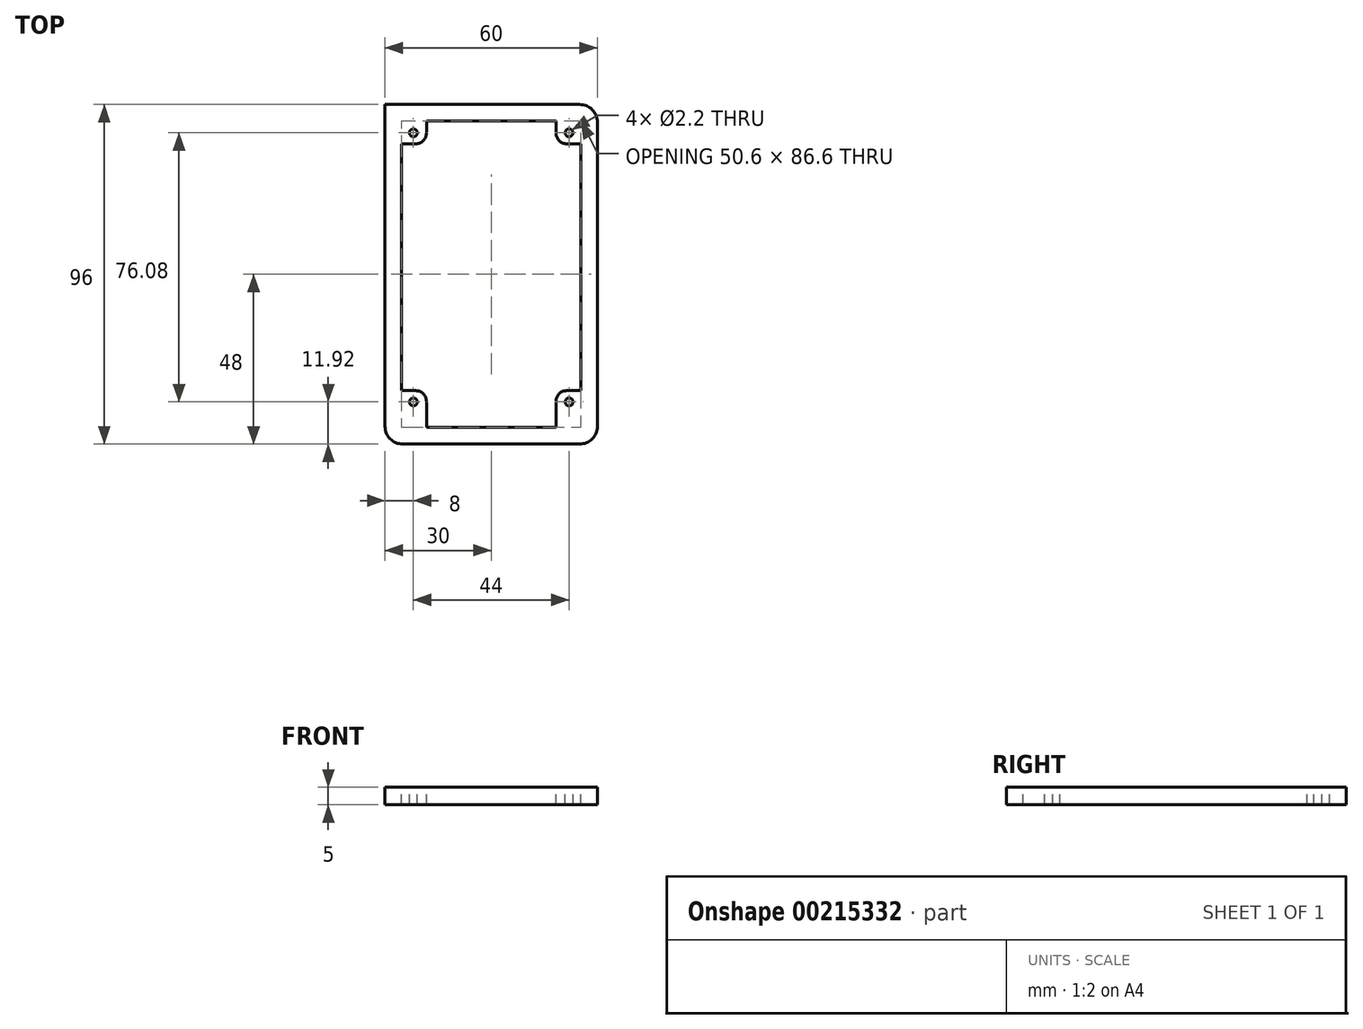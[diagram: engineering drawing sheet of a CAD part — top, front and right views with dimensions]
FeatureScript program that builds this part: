
annotation { "Feature Type Name" : "Feature", "Feature Type Description" : "" }
export const myFeature = defineFeature(function(context is Context, id is Id, definition is map)
    precondition{}
    {
        {
            var Q0;
            Q0=qCreatedBy(makeId("Top.planeOp"),FACE);
            var sketch = newSketch(context, id + "F0", { "sketchPlane" : qUnion([Q0])});
            skPoint(sketch, "E0.middle", {"position": v(0, 0) * mm});
            skCircle(sketch, "E1", {"center": v(-22, 40) * mm, "radius": 1.5 * mm});
            skCircle(sketch, "E2", {"center": v(22, 40) * mm, "radius": 1.5 * mm});
            skCircle(sketch, "E3", {"center": v(-22, -36.08) * mm, "radius": 1.5 * mm});
            skCircle(sketch, "E4", {"center": v(22, -36.08) * mm, "radius": 1.5 * mm});
            skLineSegment(sketch, "E5.bottom", {"start": v(25, -48) * mm, "end": v(-25, -48) * mm});
            skLineSegment(sketch, "E5.top", {"start": v(25, 48) * mm, "end": v(-27, 48) * mm});
            skLineSegment(sketch, "E5.left", {"start": v(30, -43) * mm, "end": v(30, 43) * mm});
            skLineSegment(sketch, "E5.right", {"start": v(-30, -43) * mm, "end": v(-30, 43) * mm});
            skPoint(sketch, "E6.visualSharp", {"position": v(-30, 48) * mm});
            skPoint(sketch, "E7.visualSharp", {"position": v(30, 48) * mm});
            skLineSegment(sketch, "E8.top", {"start": v(-30, 48) * mm, "end": v(-27, 48) * mm});
            skLineSegment(sketch, "E8.left", {"start": v(-30, 43) * mm, "end": v(-30, 48) * mm});
            skArc(sketch, "E9.filletArc", {"start": v(30, 43) * mm, "mid": v(28.54, 46.54) * mm, "end": v(25, 48) * mm});
            skPoint(sketch, "E10.visualSharp", {"position": v(30, -48) * mm});
            skArc(sketch, "E10.filletArc", {"start": v(25, -48) * mm, "mid": v(28.54, -46.54) * mm, "end": v(30, -43) * mm});
            skPoint(sketch, "E11.visualSharp", {"position": v(-30, -48) * mm});
            skArc(sketch, "E11.filletArc", {"start": v(-30, -43) * mm, "mid": v(-28.54, -46.54) * mm, "end": v(-25, -48) * mm});
            skSolve(sketch);
        }
        {
            var Q0;
            Q0=qSketchRegion(id+"F0",true);
            extrude(context, id + "F1", {"entities" : qUnion([Q0]), "depth" : 15 * mm});
        }
        {
            var Q0;
            Q0=makeQuery(id+"F1.opExtrude","CAP_FACE",FACE,{"disambiguationData":[OSD([sQuery(id+"F0.wireOp",EDGE,"E1"),sQuery(id+"F0.wireOp",EDGE,"E2"),sQuery(id+"F0.wireOp",EDGE,"E3"),sQuery(id+"F0.wireOp",EDGE,"E4"),sQuery(id+"F0.wireOp",EDGE,"E5.bottom"),sQuery(id+"F0.wireOp",EDGE,"E5.top"),sQuery(id+"F0.wireOp",EDGE,"E5.left"),sQuery(id+"F0.wireOp",EDGE,"E5.right")])],"isStart":false});
            var sketch = newSketch(context, id + "F2", { "sketchPlane" : qUnion([Q0])});
            skLineSegment(sketch, "E12.bottom", {"start": v(-25.3, 43.3) * mm, "end": v(25.3, 43.3) * mm});
            skLineSegment(sketch, "E12.top", {"start": v(-25.3, -43.3) * mm, "end": v(25.3, -43.3) * mm});
            skLineSegment(sketch, "E12.left", {"start": v(-25.3, 43.3) * mm, "end": v(-25.3, -43.3) * mm});
            skLineSegment(sketch, "E12.right", {"start": v(25.3, 43.3) * mm, "end": v(25.3, -43.3) * mm});
            skPoint(sketch, "E12.middle", {"position": v(0, 0) * mm});
            skCircle(sketch, "E13", {"center": v(-22, 40) * mm, "radius": 1.5 * mm});
            skCircle(sketch, "E14", {"center": v(22, 40) * mm, "radius": 1.5 * mm});
            skCircle(sketch, "E15", {"center": v(-22, -36.08) * mm, "radius": 1.5 * mm});
            skCircle(sketch, "E16", {"center": v(22, -36.08) * mm, "radius": 1.5 * mm});
            skSolve(sketch);
        }
        {
            var Q0;
            Q0=qSketchRegion(id+"F2",true);
            extrude(context, id + "F3", {"entities" : qUnion([Q0]), "operationType" : NewBodyOperationType.REMOVE, "oppositeDirection" : true, "depth" : 22 * mm});
        }
        {
            var Q0;
            Q0=makeQuery(id+"F1.opExtrude","CAP_FACE",FACE,{"disambiguationData":[OSD([sQuery(id+"F0.wireOp",EDGE,"E1"),sQuery(id+"F0.wireOp",EDGE,"E2"),sQuery(id+"F0.wireOp",EDGE,"E3"),sQuery(id+"F0.wireOp",EDGE,"E4"),sQuery(id+"F0.wireOp",EDGE,"E5.bottom"),sQuery(id+"F0.wireOp",EDGE,"E5.top"),sQuery(id+"F0.wireOp",EDGE,"E5.left"),sQuery(id+"F0.wireOp",EDGE,"E5.right")])],"isStart":false});
            var sketch = newSketch(context, id + "F4", { "sketchPlane" : qUnion([Q0])});
            skCircle(sketch, "E17", {"center": v(-22, 40) * mm, "radius": 1.1 * mm});
            skCircle(sketch, "E18", {"center": v(22, 40) * mm, "radius": 1.1 * mm});
            skCircle(sketch, "E19", {"center": v(22, -36.08) * mm, "radius": 1.1 * mm});
            skCircle(sketch, "E20", {"center": v(-22, -36.08) * mm, "radius": 1.1 * mm});
            skLineSegment(sketch, "E21.bottom", {"start": v(-25.3, 43.3) * mm, "end": v(-18.3, 43.3) * mm});
            skLineSegment(sketch, "E21.top", {"start": v(-25.3, 36.9) * mm, "end": v(-21.3, 36.9) * mm});
            skLineSegment(sketch, "E21.left", {"start": v(-25.3, 43.3) * mm, "end": v(-25.3, 36.9) * mm});
            skLineSegment(sketch, "E21.right", {"start": v(-18.3, 43.3) * mm, "end": v(-18.3, 39.9) * mm});
            skPoint(sketch, "E22.visualSharp", {"position": v(-18.3, 36.9) * mm});
            skArc(sketch, "E22.filletArc", {"start": v(-21.3, 36.9) * mm, "mid": v(-19.18, 37.78) * mm, "end": v(-18.3, 39.9) * mm});
            skLineSegment(sketch, "E23.bottom", {"start": v(25.3, 43.3) * mm, "end": v(18.3, 43.3) * mm});
            skLineSegment(sketch, "E23.top", {"start": v(25.3, 36.9) * mm, "end": v(21.3, 36.9) * mm});
            skLineSegment(sketch, "E23.left", {"start": v(25.3, 43.3) * mm, "end": v(25.3, 36.9) * mm});
            skLineSegment(sketch, "E23.right", {"start": v(18.3, 43.3) * mm, "end": v(18.3, 39.9) * mm});
            skPoint(sketch, "E24.visualSharp", {"position": v(18.3, 36.9) * mm});
            skArc(sketch, "E24.filletArc", {"start": v(18.3, 39.9) * mm, "mid": v(19.18, 37.78) * mm, "end": v(21.3, 36.9) * mm});
            skLineSegment(sketch, "E25.bottom", {"start": v(25.3, -43.3) * mm, "end": v(18.3, -43.3) * mm});
            skLineSegment(sketch, "E25.top", {"start": v(25.3, -32.9) * mm, "end": v(21.3, -32.9) * mm});
            skLineSegment(sketch, "E25.left", {"start": v(25.3, -43.3) * mm, "end": v(25.3, -32.9) * mm});
            skLineSegment(sketch, "E25.right", {"start": v(18.3, -43.3) * mm, "end": v(18.3, -35.9) * mm});
            skPoint(sketch, "E26.visualSharp", {"position": v(18.3, -32.9) * mm});
            skArc(sketch, "E26.filletArc", {"start": v(21.3, -32.9) * mm, "mid": v(19.18, -33.78) * mm, "end": v(18.3, -35.9) * mm});
            skLineSegment(sketch, "E27.bottom", {"start": v(-25.3, -43.3) * mm, "end": v(-18.3, -43.3) * mm});
            skLineSegment(sketch, "E27.top", {"start": v(-25.3, -32.9) * mm, "end": v(-21.3, -32.9) * mm});
            skLineSegment(sketch, "E27.left", {"start": v(-25.3, -43.3) * mm, "end": v(-25.3, -32.9) * mm});
            skLineSegment(sketch, "E27.right", {"start": v(-18.3, -43.3) * mm, "end": v(-18.3, -35.9) * mm});
            skPoint(sketch, "E28.visualSharp", {"position": v(-18.3, -32.9) * mm});
            skArc(sketch, "E28.filletArc", {"start": v(-18.3, -35.9) * mm, "mid": v(-19.18, -33.78) * mm, "end": v(-21.3, -32.9) * mm});
            skPoint(sketch, "E29.middle", {"position": v(0, 2) * mm});
            skPoint(sketch, "E29.left.start.orphan", {"position": v(-25, 36.6) * mm});
            skPoint(sketch, "E29.right.start.orphan", {"position": v(25, 36.6) * mm});
            skPoint(sketch, "E29.top.end.orphan", {"position": v(25, -32.6) * mm});
            skPoint(sketch, "E29.top.start.orphan", {"position": v(-25, -32.6) * mm});
            skSolve(sketch);
        }
        {
            var Q0;
            Q0=qSketchRegion(id+"F4",true);
            extrude(context, id + "F5", {"entities" : qUnion([Q0]), "operationType" : NewBodyOperationType.ADD, "oppositeDirection" : true, "depth" : 5 * mm});
        }
        {
            var Q0;
            Q0=makeQuery(id+"F1.opExtrude","CAP_FACE",FACE,{"disambiguationData":[OSD([sQuery(id+"F0.wireOp",EDGE,"E1"),sQuery(id+"F0.wireOp",EDGE,"E2"),sQuery(id+"F0.wireOp",EDGE,"E3"),sQuery(id+"F0.wireOp",EDGE,"E4"),sQuery(id+"F0.wireOp",EDGE,"E5.bottom"),sQuery(id+"F0.wireOp",EDGE,"E5.top"),sQuery(id+"F0.wireOp",EDGE,"E5.left"),sQuery(id+"F0.wireOp",EDGE,"E5.right"),sQuery(id+"F0.wireOp",EDGE,"E8.top"),sQuery(id+"F0.wireOp",EDGE,"E8.left"),sQuery(id+"F0.wireOp",EDGE,"E9.filletArc"),sQuery(id+"F0.wireOp",EDGE,"E10.filletArc"),sQuery(id+"F0.wireOp",EDGE,"E11.filletArc")])],"isStart":true});
            var sketch = newSketch(context, id + "F6", { "sketchPlane" : qUnion([Q0])});
            skLineSegment(sketch, "E30.bottom", {"start": v(47.14, 85.56) * mm, "end": v(-58.71, 85.56) * mm});
            skLineSegment(sketch, "E30.top", {"start": v(47.14, -95.34) * mm, "end": v(-58.71, -95.34) * mm});
            skLineSegment(sketch, "E30.left", {"start": v(47.14, 85.56) * mm, "end": v(47.14, -95.34) * mm});
            skLineSegment(sketch, "E30.right", {"start": v(-58.71, 85.56) * mm, "end": v(-58.71, -95.34) * mm});
            skSolve(sketch);
        }
        {
            var Q0;
            Q0=qSketchRegion(id+"F6",true);
            extrude(context, id + "F7", {"entities" : qUnion([Q0]), "operationType" : NewBodyOperationType.REMOVE, "oppositeDirection" : true, "depth" : 10 * mm});
        }
    });
